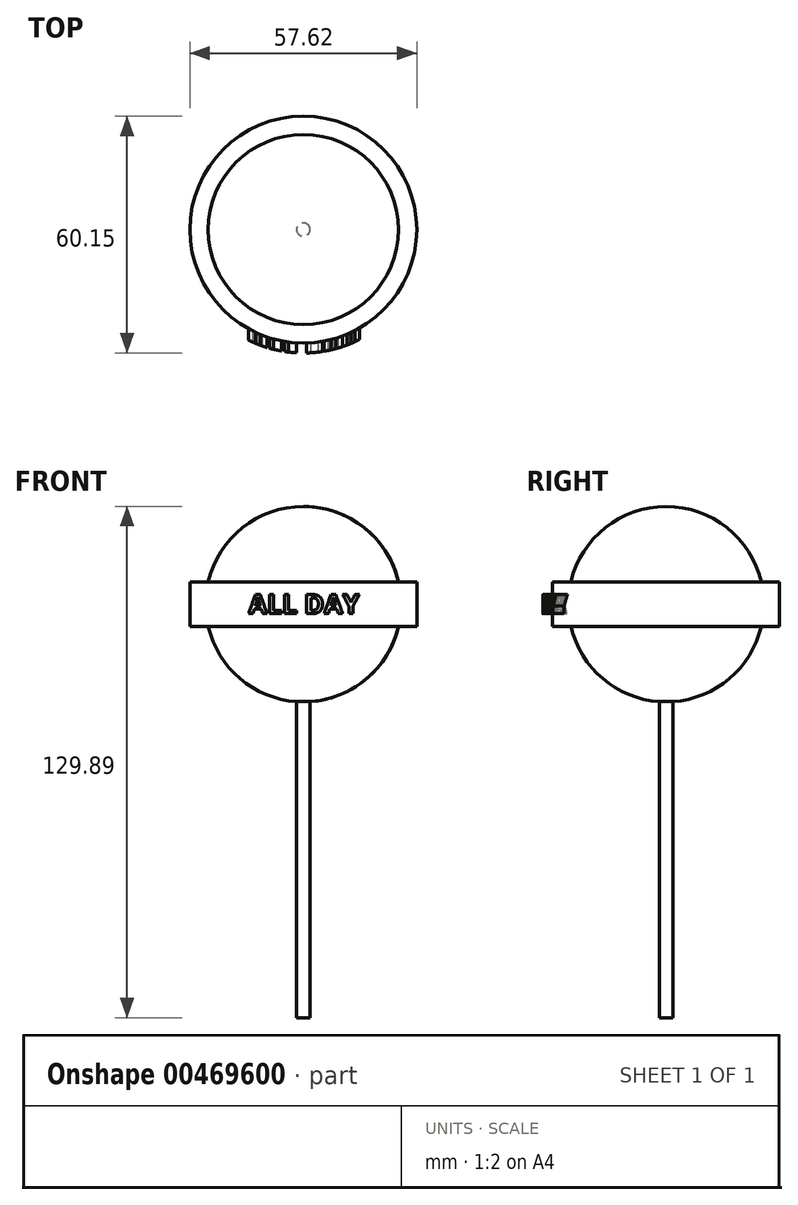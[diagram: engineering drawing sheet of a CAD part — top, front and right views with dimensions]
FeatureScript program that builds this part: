
annotation { "Feature Type Name" : "Feature", "Feature Type Description" : "" }
export const myFeature = defineFeature(function(context is Context, id is Id, definition is map)
    precondition{}
    {
        {
            var Q0;
            Q0=qCreatedBy(makeId("Front.planeOp"),FACE);
            var sketch = newSketch(context, id + "F0", { "sketchPlane" : qUnion([Q0])});
            skArc(sketch, "E0", {"start": v(0, -24.82) * mm, "mid": v(24.82, 0) * mm, "end": v(0, 24.82) * mm});
            skLineSegment(sketch, "E1", {"start": v(0, 24.82) * mm, "end": v(0, -24.82) * mm});
            skLineSegment(sketch, "E2", {"start": v(0, 50.72) * mm, "end": v(0, -46.42) * mm, "construction": true});
            skLineSegment(sketch, "E3.bottom", {"start": v(0.43, 5.66) * mm, "end": v(28.8, 5.66) * mm});
            skLineSegment(sketch, "E3.top", {"start": v(0.43, -5.66) * mm, "end": v(28.8, -5.66) * mm});
            skLineSegment(sketch, "E3.left", {"start": v(0.43, 5.66) * mm, "end": v(0.43, -5.66) * mm});
            skLineSegment(sketch, "E3.right", {"start": v(28.8, 5.66) * mm, "end": v(28.8, -5.66) * mm});
            skPoint(sketch, "E3.middle", {"position": v(14.62, 0) * mm});
            skLineSegment(sketch, "E4.bottom", {"start": v(0, -16.1) * mm, "end": v(1.7, -16.1) * mm});
            skLineSegment(sketch, "E4.top", {"start": v(0, -105.07) * mm, "end": v(1.7, -105.07) * mm});
            skLineSegment(sketch, "E4.left", {"start": v(0, -16.1) * mm, "end": v(0, -105.07) * mm});
            skLineSegment(sketch, "E4.right", {"start": v(1.7, -16.1) * mm, "end": v(1.7, -105.07) * mm});
            skSolve(sketch);
        }
        {
            var Q0;
            Q0 = qSketchRegion(id + "F0", true);
            var Q1;
            Q1=sQuery(id+"F0.wireOp",EDGE,"E2");
            revolve(context, id + "F1", {"entities" : qUnion([Q0]), "axis" : qUnion([Q1]), "revolveType" : RevolveType.FULL});
        }
        {
            var Q0;
            Q0=qCreatedBy(makeId("Front.planeOp"),FACE);
            var sketch = newSketch(context, id + "F2", { "sketchPlane" : qUnion([Q0])});
            skText(sketch, "E5", { "text": "ALL DAY", "fontName": "OpenSans-Bold.ttf"});
            const initialGuessF2  = {"E5": [-0.01391, -0.00242, 1, 0, 0.0049]};
            skSetInitialGuess(sketch, initialGuessF2);
            skSolve(sketch);
        }
        {
            var Q0;
            Q0 = qSketchRegion(id + "F2", true);
            extrude(context, id + "F3", {"entities" : qUnion([Q0]), "operationType" : NewBodyOperationType.ADD, "depth" : 45.72 * mm});
        }
        {
            var Q0;
            Q0=qCreatedBy(makeId("Front.planeOp"),FACE);
            var sketch = newSketch(context, id + "F4", { "sketchPlane" : qUnion([Q0])});
            skLineSegment(sketch, "E6", {"start": v(28.8, 5.66) * mm, "end": v(28.8, -5.66) * mm});
            skLineSegment(sketch, "E7.0", {"start": v(-28.8, 5.66) * mm, "end": v(28.8, 5.66) * mm});
            skLineSegment(sketch, "E8.0", {"start": v(-28.8, -5.66) * mm, "end": v(28.8, -5.66) * mm});
            skLineSegment(sketch, "E9.0", {"start": v(-28.8, -8.2) * mm, "end": v(31.35, -8.2) * mm});
            skLineSegment(sketch, "E9.1", {"start": v(31.35, 8.2) * mm, "end": v(31.35, -8.2) * mm});
            skLineSegment(sketch, "E9.2", {"start": v(-28.8, 8.2) * mm, "end": v(31.35, 8.2) * mm});
            skLineSegment(sketch, "E10", {"start": v(28.8, 8.2) * mm, "end": v(19.1, 18.58) * mm});
            skLineSegment(sketch, "E11", {"start": v(19.1, 18.58) * mm, "end": v(42.92, 18.58) * mm});
            skLineSegment(sketch, "E12", {"start": v(42.92, 18.58) * mm, "end": v(52.34, 0) * mm});
            skLineSegment(sketch, "E13", {"start": v(52.34, 0) * mm, "end": v(44.49, -23.2) * mm});
            skLineSegment(sketch, "E14", {"start": v(44.49, -23.2) * mm, "end": v(23.02, -23.2) * mm});
            skLineSegment(sketch, "E15", {"start": v(23.02, -23.2) * mm, "end": v(28.8, -8.2) * mm});
            skSolve(sketch);
        }
        {
            var Q0;
            Q0=qCreatedBy(makeId("Front.planeOp"),FACE);
            var sketch = newSketch(context, id + "F5", { "sketchPlane" : qUnion([Q0])});
            skLineSegment(sketch, "E16", {"start": v(0, 40.83) * mm, "end": v(0, -43.75) * mm, "construction": true});
            skSolve(sketch);
        }
        {
            var Q0;
            Q0 = qSketchRegion(id + "F4", true);
            var Q1;
            Q1=sQuery(id+"F5.wireOp",EDGE,"E16");
            revolve(context, id + "F6", {"operationType" : NewBodyOperationType.REMOVE, "entities" : qUnion([Q0]), "axis" : qUnion([Q1]), "revolveType" : RevolveType.FULL, "oppositeDirection" : true});
        }
    });
